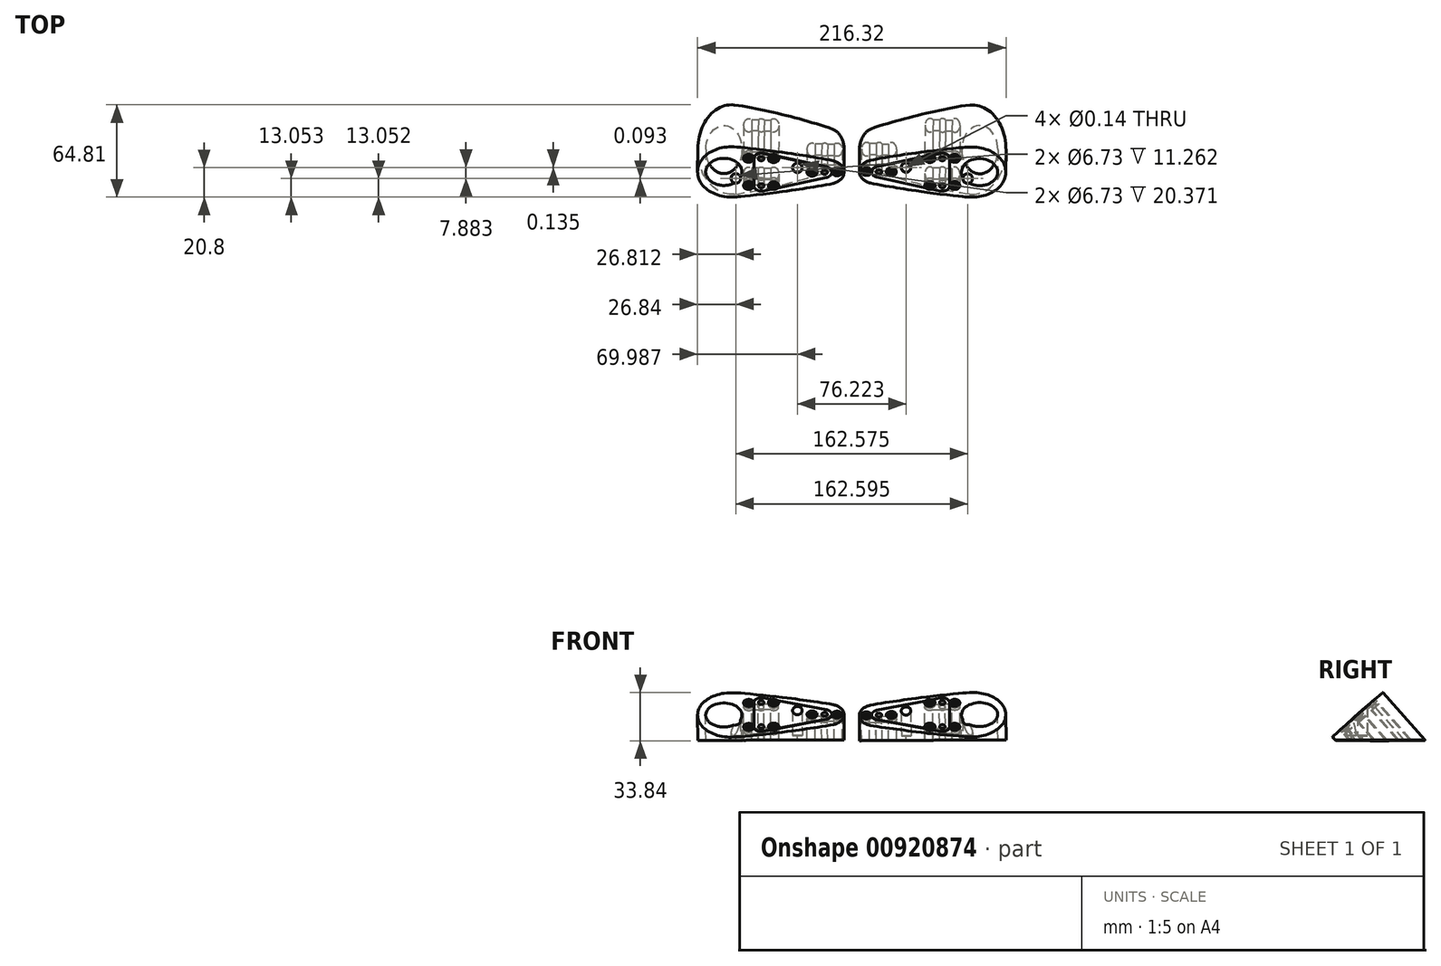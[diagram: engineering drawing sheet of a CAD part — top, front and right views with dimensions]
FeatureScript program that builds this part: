
annotation { "Feature Type Name" : "Feature", "Feature Type Description" : "" }
export const myFeature = defineFeature(function(context is Context, id is Id, definition is map)
    precondition{}
    {
        {
            assignVariable(context, id + "F0", {"name" : "wingtip_angle", "anyValue" : 41.5 * degree});
        }
        {
            assignVariable(context, id + "F1", {"name" : "RivetDiam", "anyValue" : .136});
        }
        {
            var Q0;
            Q0=qCreatedBy(makeId("Right.planeOp"),FACE);
            var sketch = newSketch(context, id + "F2", { "sketchPlane" : qUnion([Q0])});
            skLineSegment(sketch, "E0", {"start": v(29.81, -35.47) * mm, "end": v(29.81, 66.13) * mm, "construction": true});
            skSolve(sketch);
        }
        {
            var Q0;
            Q0=qCreatedBy(makeId("Right.planeOp"),FACE);
            var sketch = newSketch(context, id + "F3", { "sketchPlane" : qUnion([Q0])});
            skLineSegment(sketch, "E1.0", {"start": v(29.81, 66.13) * mm, "end": v(29.81, -36.61) * mm, "construction": true});
            skCircle(sketch, "E2", {"center": v(29.81, 52.41) * mm, "radius": 1.97 * mm});
            skCircle(sketch, "E3", {"center": v(17.11, 7.96) * mm, "radius": 1.97 * mm});
            skCircle(sketch, "E4.MirrorC", {"center": v(42.51, 7.96) * mm, "radius": 1.97 * mm});
            skCircle(sketch, "E5", {"center": v(29.81, -18.2) * mm, "radius": 12.7 * mm});
            skArc(sketch, "E6", {"start": v(6.4, -11.13) * mm, "mid": v(29.81, -36.61) * mm, "end": v(53.22, -11.13) * mm});
            skArc(sketch, "E7", {"start": v(40.44, 58.4) * mm, "mid": v(29.81, 66.13) * mm, "end": v(19.18, 58.4) * mm});
            skPoint(sketch, "E8", {"position": v(43.4, 46.44) * mm});
            skPoint(sketch, "E9", {"position": v(45.73, 35.59) * mm});
            skPoint(sketch, "E10", {"position": v(48.91, 18.93) * mm});
            skPoint(sketch, "E11", {"position": v(52.95, -7.22) * mm});
            skFitSpline(sketch, "E12", {"points": [v(53.22, -11.13) * mm, v(52.95, -7.22) * mm, v(48.91, 18.93) * mm, v(45.73, 35.59) * mm, v(43.4, 46.44) * mm, v(40.44, 58.4) * mm], "startDerivative": vector(-6.09, 71.8) * mm, "endDerivative": vector(-14.94, 46.1) * mm});
            skFitSpline(sketch, "E13.MirrorCS", {"points": [v(6.4, -11.13) * mm, v(6.67, -7.22) * mm, v(10.71, 18.93) * mm, v(13.9, 35.59) * mm, v(16.22, 46.44) * mm, v(19.18, 58.4) * mm], "startDerivative": vector(6.09, 71.8) * mm, "endDerivative": vector(14.94, 46.1) * mm});
            skLineSegment(sketch, "E14", {"start": v(50.72, 7.96) * mm, "end": v(8.9, 7.96) * mm, "construction": true});
            skSolve(sketch);
        }
        {
            var Q0;
            Q0=sQuery(id+"F3.wireOp",EDGE,"E1.0");
            cPlane(context, id + "F4", {"entities" : qUnion([Q0]), "cplaneType" : CPlaneType.LINE_ANGLE, "offset" : 25.4 * mm, "angle" : getVariable(context, 'wingtip_angle'), "width" : 152.4 * mm, "height" : 152.4 * mm});
        }
        {
            var Q0;
            Q0=qCreatedBy(id+"F4.planeOp",FACE);
            cPlane(context, id + "F5", {"entities" : qUnion([Q0]), "cplaneType" : CPlaneType.OFFSET, "offset" : 17.78 * mm, "width" : 152.4 * mm, "height" : 152.4 * mm});
        }
        {
            var Q0;
            Q0=qSketchRegion(id+"F3",true);
            var Q1;
            Q1=qCreatedBy(id+"F5.planeOp",FACE);
            extrude(context, id + "F6", {"entities" : qUnion([Q0]), "endBound" : BoundingType.UP_TO_SURFACE, "oppositeDirection" : true, "depth" : 50.8 * mm, "endBoundEntityFace" : qUnion([Q1]), "offsetDistance" : 25.4 * mm});
        }
        {
            var Q0;
            Q0=makeQuery(id+"F6.opExtrude","CAP_FACE",FACE,{"disambiguationData":[OSD([sQuery(id+"F3.wireOp",EDGE,"E2"),sQuery(id+"F3.wireOp",EDGE,"E3"),sQuery(id+"F3.wireOp",EDGE,"E4.MirrorC"),sQuery(id+"F3.wireOp",EDGE,"E5"),sQuery(id+"F3.wireOp",EDGE,"E6"),sQuery(id+"F3.wireOp",EDGE,"E7"),sQuery(id+"F3.wireOp",EDGE,"E12"),sQuery(id+"F3.wireOp",EDGE,"E13.MirrorCS")])],"isStart":false});
            var sketch = newSketch(context, id + "F7", { "sketchPlane" : qUnion([Q0])});
            skPoint(sketch, "E15", {"position": v(-19.18, 33.36) * mm});
            skCircle(sketch, "E16", {"center": v(-19.18, 33.36) * mm, "radius": 3.37 * mm});
            skEllipse(sketch, "E17.0", {"center": v(-6.6, 52.41) * mm, "majorRadius": 2.63 * mm, "minorRadius": 1.97 * mm, "majorAxis": v(-1, 0), "construction": true});
            skEllipse(sketch, "E18.0", {"center": v(10.36, 7.96) * mm, "majorRadius": 2.63 * mm, "minorRadius": 1.97 * mm, "majorAxis": v(-1, 0), "construction": true});
            skEllipse(sketch, "E19.0", {"center": v(-23.56, 7.96) * mm, "majorRadius": 2.63 * mm, "minorRadius": 1.97 * mm, "majorAxis": v(-1, 0), "construction": true});
            skLineSegment(sketch, "E20", {"start": v(-23.56, 7.96) * mm, "end": v(10.36, 7.96) * mm, "construction": true});
            skLineSegment(sketch, "E21", {"start": v(-6.6, 52.41) * mm, "end": v(0, 7.96) * mm, "construction": true});
            skPoint(sketch, "E22", {"position": v(-26.9, -9.82) * mm});
            skCircle(sketch, "E23", {"center": v(-26.9, -9.82) * mm, "radius": 3.37 * mm});
            skSolve(sketch);
        }
        {
            var Q0;
            Q0=sQuery(id+"F7.wireOp",VERTEX,"E15");
            var Q1;
            Q1=sQuery(id+"F7.wireOp",VERTEX,"b06482be-c945-4cb5-a45d-5072c32f2ec3");
            var Q2;
            Q2=sQuery(id+"F7.wireOp",VERTEX,"342dbf68-9167-48f7-8551-4fa16eff7878");
            var Q3;
            Q3=sQuery(id+"F7.wireOp",VERTEX,"215f591c-f985-48cd-a801-7776d395aa3d");
            var Q4;
            Q4=sQuery(id+"F7.wireOp",VERTEX,"E22");
            var Q5;
            Q5=makeQuery(id+"FviUrEG43XHwvwd_1.splitOp","SPLIT",BODY,{"derivedFrom":makeQuery(id+"F6.opExtrude","SWEPT_BODY",BODY,{"disambiguationData":[OSD([sQuery(id+"F3.wireOp",EDGE,"E2"),sQuery(id+"F3.wireOp",EDGE,"5mLEWZTt-4N4c-xanL-msg1-CrMGUHAulQAG"),sQuery(id+"F3.wireOp",EDGE,"E3"),sQuery(id+"F3.wireOp",EDGE,"E4.MirrorC"),sQuery(id+"F3.wireOp",EDGE,"a63d0188-a2c3-4da0-82b0-e67cc7725ef2")])]}),"isFromBackBody":true});
            hole(context, id + "F8", {"style" : HoleStyle.SIMPLE, "endStyle" : HoleEndStyle.THROUGH, "holeDiameter" : (getVariable(context, 'RivetDiam')) * mm, "majorDiameter" : 6.35 * mm, "isTappedThrough" : true, "tappedDepth" : 12.7 * mm, "tapClearance" : 3, "locations" : qUnion([Q0, Q1, Q2, Q3, Q4]), "scope" : qUnion([Q5]), "startStyle" : HoleStartStyle.PART});
        }
        {
            var Q0;
            Q0=qSketchRegion(id+"F7",true);
            extrude(context, id + "F9", {"entities" : qUnion([Q0]), "operationType" : NewBodyOperationType.REMOVE, "endBound" : BoundingType.THROUGH_ALL, "oppositeDirection" : true, "depth" : 25.4 * mm, "offsetDistance" : 25.4 * mm, "hasSecondDirection" : true, "secondDirectionOppositeDirection" : true, "secondDirectionDepth" : 3.17 * mm});
        }
        {
            var Q0;
            Q0=makeQuery(id+"F6.opExtrude","CAP_FACE",FACE,{"disambiguationData":[OSD([sQuery(id+"F3.wireOp",EDGE,"E2"),sQuery(id+"F3.wireOp",EDGE,"5mLEWZTt-4N4c-xanL-msg1-CrMGUHAulQAG"),sQuery(id+"F3.wireOp",EDGE,"E3"),sQuery(id+"F3.wireOp",EDGE,"E4.MirrorC"),sQuery(id+"F3.wireOp",EDGE,"a63d0188-a2c3-4da0-82b0-e67cc7725ef2")])],"isStart":true});
            cPlane(context, id + "F10", {"entities" : qUnion([Q0]), "cplaneType" : CPlaneType.OFFSET, "offset" : 4 * mm, "oppositeDirection" : true, "width" : 152.4 * mm, "height" : 152.4 * mm});
        }
        {
            var Q0;
            Q0=qCreatedBy(id+"F10.planeOp",FACE);
            var sketch = newSketch(context, id + "F11", { "sketchPlane" : qUnion([Q0])});
            skCircle(sketch, "E24.0", {"center": v(17.11, 7.96) * mm, "radius": 1.97 * mm});
            skCircle(sketch, "E25", {"center": v(17.11, 16.7) * mm, "radius": 1.24 * mm});
            skArc(sketch, "E26", {"start": v(20, 14.64) * mm, "mid": v(17.11, 20.26) * mm, "end": v(14.22, 14.64) * mm});
            skArc(sketch, "E27", {"start": v(14.22, 10.03) * mm, "mid": v(13.56, 7.96) * mm, "end": v(14.22, 5.9) * mm});
            skLineSegment(sketch, "E28", {"start": v(20, 14.64) * mm, "end": v(20, 10.03) * mm});
            skLineSegment(sketch, "E29", {"start": v(14.22, 14.64) * mm, "end": v(14.22, 10.03) * mm});
            skArc(sketch, "E30.MirrorCS", {"start": v(14.22, 5.9) * mm, "mid": v(13.56, 7.96) * mm, "end": v(14.22, 10.03) * mm});
            skLineSegment(sketch, "E31.MirrorCS", {"start": v(14.22, 1.3) * mm, "end": v(14.22, 5.9) * mm});
            skArc(sketch, "E32.MirrorCS", {"start": v(20, 1.3) * mm, "mid": v(17.11, -4.33) * mm, "end": v(14.22, 1.3) * mm});
            skLineSegment(sketch, "E33.MirrorCS", {"start": v(20, 1.3) * mm, "end": v(20, 5.9) * mm});
            skArc(sketch, "E34.trimOffspring", {"start": v(20, 10.03) * mm, "mid": v(20.67, 7.96) * mm, "end": v(20, 5.9) * mm});
            skArc(sketch, "E35.trimOffspring", {"start": v(20, 5.9) * mm, "mid": v(20.67, 7.96) * mm, "end": v(20, 10.03) * mm});
            skLineSegment(sketch, "E36", {"start": v(17.11, 16.7) * mm, "end": v(17.11, -0.77) * mm, "construction": true});
            skCircle(sketch, "E37.MirrorC", {"center": v(17.11, -0.77) * mm, "radius": 1.24 * mm});
            skCircle(sketch, "E38.0", {"center": v(29.81, 52.41) * mm, "radius": 1.97 * mm});
            skCircle(sketch, "E39", {"center": v(29.81, 61.15) * mm, "radius": 1.24 * mm});
            skArc(sketch, "E40", {"start": v(32.7, 59.09) * mm, "mid": v(29.81, 64.7) * mm, "end": v(26.92, 59.09) * mm});
            skArc(sketch, "E41", {"start": v(26.92, 54.48) * mm, "mid": v(26.26, 52.41) * mm, "end": v(26.92, 50.35) * mm});
            skLineSegment(sketch, "E42", {"start": v(32.7, 59.09) * mm, "end": v(32.7, 54.48) * mm});
            skLineSegment(sketch, "E43", {"start": v(26.92, 59.09) * mm, "end": v(26.92, 54.48) * mm});
            skArc(sketch, "E44.MirrorCS", {"start": v(26.92, 50.35) * mm, "mid": v(26.26, 52.41) * mm, "end": v(26.92, 54.48) * mm});
            skLineSegment(sketch, "E45.MirrorCS", {"start": v(26.92, 45.74) * mm, "end": v(26.92, 50.35) * mm});
            skArc(sketch, "E46.MirrorCS", {"start": v(32.7, 45.74) * mm, "mid": v(29.81, 40.12) * mm, "end": v(26.92, 45.74) * mm});
            skLineSegment(sketch, "E47.MirrorCS", {"start": v(32.7, 45.74) * mm, "end": v(32.7, 50.35) * mm});
            skArc(sketch, "E48.trimOffspring", {"start": v(32.7, 54.48) * mm, "mid": v(33.37, 52.41) * mm, "end": v(32.7, 50.35) * mm});
            skArc(sketch, "E49.trimOffspring", {"start": v(32.7, 50.35) * mm, "mid": v(33.37, 52.41) * mm, "end": v(32.7, 54.48) * mm});
            skLineSegment(sketch, "E50", {"start": v(29.81, 61.15) * mm, "end": v(29.81, 43.68) * mm, "construction": true});
            skCircle(sketch, "E51.MirrorC", {"center": v(29.81, 43.68) * mm, "radius": 1.24 * mm});
            skCircle(sketch, "E52.0", {"center": v(42.51, 7.96) * mm, "radius": 1.97 * mm});
            skCircle(sketch, "E53", {"center": v(42.51, 16.7) * mm, "radius": 1.24 * mm});
            skArc(sketch, "E54", {"start": v(45.4, 14.64) * mm, "mid": v(42.51, 20.26) * mm, "end": v(39.62, 14.64) * mm});
            skArc(sketch, "E55", {"start": v(39.62, 10.03) * mm, "mid": v(38.96, 7.96) * mm, "end": v(39.62, 5.9) * mm});
            skLineSegment(sketch, "E56", {"start": v(45.4, 14.64) * mm, "end": v(45.4, 10.03) * mm});
            skLineSegment(sketch, "E57", {"start": v(39.62, 14.64) * mm, "end": v(39.62, 10.03) * mm});
            skArc(sketch, "E58.MirrorCS", {"start": v(39.62, 5.9) * mm, "mid": v(38.96, 7.96) * mm, "end": v(39.62, 10.03) * mm});
            skLineSegment(sketch, "E59.MirrorCS", {"start": v(39.62, 1.3) * mm, "end": v(39.62, 5.9) * mm});
            skArc(sketch, "E60.MirrorCS", {"start": v(45.4, 1.3) * mm, "mid": v(42.51, -4.33) * mm, "end": v(39.62, 1.3) * mm});
            skLineSegment(sketch, "E61.MirrorCS", {"start": v(45.4, 1.3) * mm, "end": v(45.4, 5.9) * mm});
            skArc(sketch, "E62.trimOffspring", {"start": v(45.4, 10.03) * mm, "mid": v(46.07, 7.96) * mm, "end": v(45.4, 5.9) * mm});
            skArc(sketch, "E63.trimOffspring", {"start": v(45.4, 5.9) * mm, "mid": v(46.07, 7.96) * mm, "end": v(45.4, 10.03) * mm});
            skLineSegment(sketch, "E64", {"start": v(42.51, 16.7) * mm, "end": v(42.51, -0.77) * mm, "construction": true});
            skCircle(sketch, "E65.MirrorC", {"center": v(42.51, -0.77) * mm, "radius": 1.24 * mm});
            skSolve(sketch);
        }
        {
            var Q0;
            Q0=qSketchRegion(id+"F11",true);
            extrude(context, id + "F12", {"entities" : qUnion([Q0]), "operationType" : NewBodyOperationType.REMOVE, "endBound" : BoundingType.THROUGH_ALL, "oppositeDirection" : true, "depth" : 25.4 * mm, "offsetDistance" : 25.4 * mm});
        }
        {
            var Q0;
            Q0=makeQuery(id+"F6.opExtrude","CAP_FACE",FACE,{"disambiguationData":[OSD([sQuery(id+"F3.wireOp",EDGE,"E2"),sQuery(id+"F3.wireOp",EDGE,"5mLEWZTt-4N4c-xanL-msg1-CrMGUHAulQAG"),sQuery(id+"F3.wireOp",EDGE,"E3"),sQuery(id+"F3.wireOp",EDGE,"E4.MirrorC"),sQuery(id+"F3.wireOp",EDGE,"a63d0188-a2c3-4da0-82b0-e67cc7725ef2")])],"isStart":true});
            var sketch = newSketch(context, id + "F13", { "sketchPlane" : qUnion([Q0])});
            skCircle(sketch, "E66", {"center": v(42.51, -0.77) * mm, "radius": 3.64 * mm});
            skCircle(sketch, "E67", {"center": v(42.51, 16.7) * mm, "radius": 3.64 * mm});
            skCircle(sketch, "E68", {"center": v(17.11, 16.7) * mm, "radius": 3.64 * mm});
            skCircle(sketch, "E69", {"center": v(17.11, -0.77) * mm, "radius": 3.64 * mm});
            skCircle(sketch, "E70", {"center": v(29.81, 43.68) * mm, "radius": 3.56 * mm});
            skCircle(sketch, "E71", {"center": v(29.81, 61.15) * mm, "radius": 3.56 * mm});
            skSolve(sketch);
        }
        {
            var Q0;
            Q0=qSketchRegion(id+"F13",true);
            extrude(context, id + "F14", {"entities" : qUnion([Q0]), "operationType" : NewBodyOperationType.REMOVE, "oppositeDirection" : true, "depth" : 1.63 * mm, "offsetDistance" : 25.4 * mm});
        }
        {
            var Q0;
            Q0=sQuery(id+"F13.wireOp",VERTEX,"E69.center");
            var Q1;
            Q1=sQuery(id+"F13.wireOp",VERTEX,"E66.center");
            var Q2;
            Q2=sQuery(id+"F13.wireOp",VERTEX,"E68.center");
            var Q3;
            Q3=sQuery(id+"F13.wireOp",VERTEX,"E67.center");
            var Q4;
            Q4=sQuery(id+"F13.wireOp",VERTEX,"E70.center");
            var Q5;
            Q5=sQuery(id+"F13.wireOp",VERTEX,"E71.center");
            var Q6;
            Q6=makeQuery(id+"FviUrEG43XHwvwd_1.splitOp","SPLIT",BODY,{"derivedFrom":makeQuery(id+"F6.opExtrude","SWEPT_BODY",BODY,{"disambiguationData":[OSD([sQuery(id+"F3.wireOp",EDGE,"E2"),sQuery(id+"F3.wireOp",EDGE,"5mLEWZTt-4N4c-xanL-msg1-CrMGUHAulQAG"),sQuery(id+"F3.wireOp",EDGE,"E3"),sQuery(id+"F3.wireOp",EDGE,"E4.MirrorC"),sQuery(id+"F3.wireOp",EDGE,"a63d0188-a2c3-4da0-82b0-e67cc7725ef2")])]}),"isFromBackBody":true});
            hole(context, id + "F15", {"style" : HoleStyle.C_SINK, "endStyle" : HoleEndStyle.THROUGH, "holeDiameter" : 2.5 * mm, "cSinkDiameter" : 4.5 * mm, "cSinkAngle" : 120 * degree, "majorDiameter" : 6.35 * mm, "isTappedThrough" : true, "tappedDepth" : 12.7 * mm, "tapClearance" : 3, "locations" : qUnion([Q0, Q1, Q2, Q3, Q4, Q5]), "scope" : qUnion([Q6]), "startStyle" : HoleStartStyle.PART});
        }
        {
            var Q0;
            Q0=makeQuery(id+"F13.imprint","IMPRINT",FACE,{"disambiguationData":[TD([[makeQuery(id+"F13.imprint","IMPRINT",EDGE,{"derivedFrom":sQuery(id+"F13.wireOp",EDGE,"E66")}),-1.0]])]});
            var sketch = newSketch(context, id + "F16", { "sketchPlane" : qUnion([Q0])});
            skPoint(sketch, "E72.0", {"position": v(29.81, 52.41) * mm});
            skPoint(sketch, "E73.0", {"position": v(42.51, 7.96) * mm});
            skPoint(sketch, "E74.0", {"position": v(17.11, 7.96) * mm});
            skArc(sketch, "E75", {"start": v(34.7, 53.81) * mm, "mid": v(29.81, 57.5) * mm, "end": v(24.93, 53.81) * mm});
            skArc(sketch, "E76", {"start": v(12.23, 9.36) * mm, "mid": v(13.06, 4.9) * mm, "end": v(17.11, 2.88) * mm});
            skArc(sketch, "E77", {"start": v(42.51, 2.88) * mm, "mid": v(46.57, 4.9) * mm, "end": v(47.4, 9.36) * mm});
            skLineSegment(sketch, "E78", {"start": v(34.7, 53.81) * mm, "end": v(44.41, 19.81) * mm});
            skLineSegment(sketch, "E79", {"start": v(24.93, 53.81) * mm, "end": v(19.84, 36.01) * mm});
            skLineSegment(sketch, "E80", {"start": v(17.11, 2.88) * mm, "end": v(42.51, 2.88) * mm});
            skCircle(sketch, "E81.0", {"center": v(29.81, 43.68) * mm, "radius": 3.56 * mm});
            skCircle(sketch, "E82.0", {"center": v(29.81, 52.41) * mm, "radius": 1.97 * mm});
            skEllipticalArc(sketch, "E83.0", {});
            skCircle(sketch, "E84.0", {"center": v(17.11, 7.96) * mm, "radius": 1.97 * mm});
            skCircle(sketch, "E85.0", {"center": v(42.51, 7.96) * mm, "radius": 1.97 * mm});
            skArc(sketch, "E86.0", {"start": v(44.41, 19.81) * mm, "mid": v(39, 15.7) * mm, "end": v(45.77, 15.06) * mm});
            skArc(sketch, "E87.0", {"start": v(13.86, 15.06) * mm, "mid": v(20.62, 15.7) * mm, "end": v(15.22, 19.81) * mm});
            skLineSegment(sketch, "E88.trimOffspring", {"start": v(18.6, 31.67) * mm, "end": v(15.22, 19.81) * mm});
            skLineSegment(sketch, "E89.trimOffspring", {"start": v(13.86, 15.06) * mm, "end": v(12.23, 9.36) * mm});
            skLineSegment(sketch, "E90.trimOffspring", {"start": v(45.77, 15.06) * mm, "end": v(47.4, 9.36) * mm});
            skLineSegment(sketch, "E91", {"start": v(19.84, 36.01) * mm, "end": v(18.6, 31.67) * mm});
            skEllipse(sketch, "E92.0", {"center": v(25.6, 33.36) * mm, "majorRadius": 4.5 * mm, "minorRadius": 3.37 * mm, "majorAxis": v(1, 0)});
            const initialGuessF16  = {"E83.0": [0.02561313730479687, 0.03333969345315713, 0.99999930665352, 0.0011775790757282112, 0.004493590083609414, 0.0033655000000000004, 3.3637215423180695, 2.6597155554827485]};
            skSetInitialGuess(sketch, initialGuessF16);
            skSolve(sketch);
        }
        {
            var Q0;
            Q0 = qSketchRegion(id + "F16", true);
            extrude(context, id + "F17", {"entities" : qUnion([Q0]), "operationType" : NewBodyOperationType.ADD, "depth" : 0.25 * mm, "offsetDistance" : 25.4 * mm});
        }
        {
            var Q0;
            Q0=makeQuery(id+"FviUrEG43XHwvwd_1.splitOp","SPLIT",BODY,{"derivedFrom":makeQuery(id+"F6.opExtrude","SWEPT_BODY",BODY,{"disambiguationData":[OSD([sQuery(id+"F3.wireOp",EDGE,"E2"),sQuery(id+"F3.wireOp",EDGE,"5mLEWZTt-4N4c-xanL-msg1-CrMGUHAulQAG"),sQuery(id+"F3.wireOp",EDGE,"E3"),sQuery(id+"F3.wireOp",EDGE,"E4.MirrorC"),sQuery(id+"F3.wireOp",EDGE,"a90b89ca-b616-4d5b-aad8-8ab6aaaaa129"),sQuery(id+"F3.wireOp",EDGE,"467a7b54-93f6-4e5c-b992-2a7b6119003c0.MirrorCS"),sQuery(id+"F3.wireOp",EDGE,"166378dd-d01e-4405-b226-b00198e31497.filletArc"),sQuery(id+"F3.wireOp",EDGE,"0c5d1a79-13bc-4d85-a67c-f0904e7e0d27.filletArc")])]}),"isFromBackBody":true});
            var Q1;
            Q1=makeQuery(id+"FviUrEG43XHwvwd_1.splitOp","SPLIT",BODY,{"derivedFrom":makeQuery(id+"F6.opExtrude","SWEPT_BODY",BODY,{"disambiguationData":[OSD([sQuery(id+"F3.wireOp",EDGE,"E2"),sQuery(id+"F3.wireOp",EDGE,"5mLEWZTt-4N4c-xanL-msg1-CrMGUHAulQAG"),sQuery(id+"F3.wireOp",EDGE,"E3"),sQuery(id+"F3.wireOp",EDGE,"E4.MirrorC"),sQuery(id+"F3.wireOp",EDGE,"a90b89ca-b616-4d5b-aad8-8ab6aaaaa129"),sQuery(id+"F3.wireOp",EDGE,"467a7b54-93f6-4e5c-b992-2a7b6119003c0.MirrorCS"),sQuery(id+"F3.wireOp",EDGE,"166378dd-d01e-4405-b226-b00198e31497.filletArc"),sQuery(id+"F3.wireOp",EDGE,"0c5d1a79-13bc-4d85-a67c-f0904e7e0d27.filletArc")])]})});
            var Q2;
            Q2=qCreatedBy(makeId("Right.planeOp"),FACE);
            mirror(context, id + "F18", {"entities" : qUnion([Q0, Q1]), "mirrorPlane" : qUnion([Q2])});
        }
        {
            var Q0;
            Q0=makeQuery(id+"F18.opPattern","COPY",BODY,{"derivedFrom":makeQuery(id+"F6.opExtrude","SWEPT_BODY",BODY,{"disambiguationData":[OSD([sQuery(id+"F3.wireOp",EDGE,"E2"),sQuery(id+"F3.wireOp",EDGE,"E3"),sQuery(id+"F3.wireOp",EDGE,"E4.MirrorC"),sQuery(id+"F3.wireOp",EDGE,"E5"),sQuery(id+"F3.wireOp",EDGE,"E6"),sQuery(id+"F3.wireOp",EDGE,"E7"),sQuery(id+"F3.wireOp",EDGE,"E12"),sQuery(id+"F3.wireOp",EDGE,"E13.MirrorCS")])]}),"instanceName":"1"});
            var Q1;
            Q1=sQuery(id+"F3.wireOp",EDGE,"E14");
            transform(context, id + "F19", {"entities" : qUnion([Q0]), "transformType" : TransformType.ROTATION, "transformAxis" : qUnion([Q1]), "angle" : 90 * degree, "makeCopy" : false});
        }
        {
            var Q0;
            Q0=makeQuery(id+"F6.opExtrude","SWEPT_BODY",BODY,{"disambiguationData":[OSD([sQuery(id+"F3.wireOp",EDGE,"E2"),sQuery(id+"F3.wireOp",EDGE,"E3"),sQuery(id+"F3.wireOp",EDGE,"E4.MirrorC"),sQuery(id+"F3.wireOp",EDGE,"E5"),sQuery(id+"F3.wireOp",EDGE,"E6"),sQuery(id+"F3.wireOp",EDGE,"E7"),sQuery(id+"F3.wireOp",EDGE,"E12"),sQuery(id+"F3.wireOp",EDGE,"E13.MirrorCS")])]});
            var Q1;
            Q1=sQuery(id+"F3.wireOp",EDGE,"E1.0");
            var Q2;
            Q2=sQuery(id+"F3.wireOp",EDGE,"E14");
            transform(context, id + "F20", {"entities" : qUnion([Q0]), "transformType" : TransformType.ROTATION, "transformAxis" : qUnion([Q2]), "angle" : 90 * degree - .221 * degree, "oppositeDirection" : true, "makeCopy" : false});
        }
        {
            var Q0;
            Q0=makeQuery(id+"F6.opExtrude","CAP_FACE",FACE,{"disambiguationData":[OSD([sQuery(id+"F3.wireOp",EDGE,"E2"),sQuery(id+"F3.wireOp",EDGE,"E3"),sQuery(id+"F3.wireOp",EDGE,"E4.MirrorC"),sQuery(id+"F3.wireOp",EDGE,"E5"),sQuery(id+"F3.wireOp",EDGE,"E6"),sQuery(id+"F3.wireOp",EDGE,"E7"),sQuery(id+"F3.wireOp",EDGE,"E12"),sQuery(id+"F3.wireOp",EDGE,"E13.MirrorCS")])],"isStart":true});
            var sketch = newSketch(context, id + "F21", { "sketchPlane" : qUnion([Q0])});
            skLineSegment(sketch, "E93", {"start": v(-53.08, -53.28) * mm, "end": v(26.27, -53.22) * mm, "construction": true});
            skLineSegment(sketch, "E94", {"start": v(0.03, 26.76) * mm, "end": v(-0.02, 7.74) * mm, "construction": true});
            skSolve(sketch);
        }
        {
            var Q0;
            Q0=makeQuery(id+"F6.opExtrude","SWEPT_BODY",BODY,{"disambiguationData":[OSD([sQuery(id+"F3.wireOp",EDGE,"E2"),sQuery(id+"F3.wireOp",EDGE,"E3"),sQuery(id+"F3.wireOp",EDGE,"E4.MirrorC"),sQuery(id+"F3.wireOp",EDGE,"E5"),sQuery(id+"F3.wireOp",EDGE,"E6"),sQuery(id+"F3.wireOp",EDGE,"E7"),sQuery(id+"F3.wireOp",EDGE,"E12"),sQuery(id+"F3.wireOp",EDGE,"E13.MirrorCS")])]});
            var Q1;
            Q1=makeQuery(id+"F18.opPattern","COPY",BODY,{"derivedFrom":makeQuery(id+"F6.opExtrude","SWEPT_BODY",BODY,{"disambiguationData":[OSD([sQuery(id+"F3.wireOp",EDGE,"E2"),sQuery(id+"F3.wireOp",EDGE,"E3"),sQuery(id+"F3.wireOp",EDGE,"E4.MirrorC"),sQuery(id+"F3.wireOp",EDGE,"E5"),sQuery(id+"F3.wireOp",EDGE,"E6"),sQuery(id+"F3.wireOp",EDGE,"E7"),sQuery(id+"F3.wireOp",EDGE,"E12"),sQuery(id+"F3.wireOp",EDGE,"E13.MirrorCS")])]}),"instanceName":"1"});
            var Q2;
            Q2=sQuery(id+"F21.wireOp",EDGE,"E93");
            var Q3;
            Q3=sQuery(id+"F21.wireOp",EDGE,"E93");
            transform(context, id + "F22", {"entities" : qUnion([Q0, Q1]), "transformType" : TransformType.ROTATION, "transformAxis" : qUnion([Q3]), "angle" : getVariable(context, 'wingtip_angle') + 180 * degree, "makeCopy" : false});
        }
        {
            var Q0;
            Q0=makeQuery(id+"F18.opPattern","COPY",BODY,{"derivedFrom":makeQuery(id+"F6.opExtrude","SWEPT_BODY",BODY,{"disambiguationData":[OSD([sQuery(id+"F3.wireOp",EDGE,"E2"),sQuery(id+"F3.wireOp",EDGE,"E3"),sQuery(id+"F3.wireOp",EDGE,"E4.MirrorC"),sQuery(id+"F3.wireOp",EDGE,"E5"),sQuery(id+"F3.wireOp",EDGE,"E6"),sQuery(id+"F3.wireOp",EDGE,"E7"),sQuery(id+"F3.wireOp",EDGE,"E12"),sQuery(id+"F3.wireOp",EDGE,"E13.MirrorCS")])]}),"instanceName":"1"});
            transform(context, id + "F23", {"entities" : qUnion([Q0]), "transformType" : TransformType.TRANSLATION_3D, "dx" : 127 * mm, "dy" : 0 * mm, "dz" : 0 * mm, "makeCopy" : false});
        }
    });
